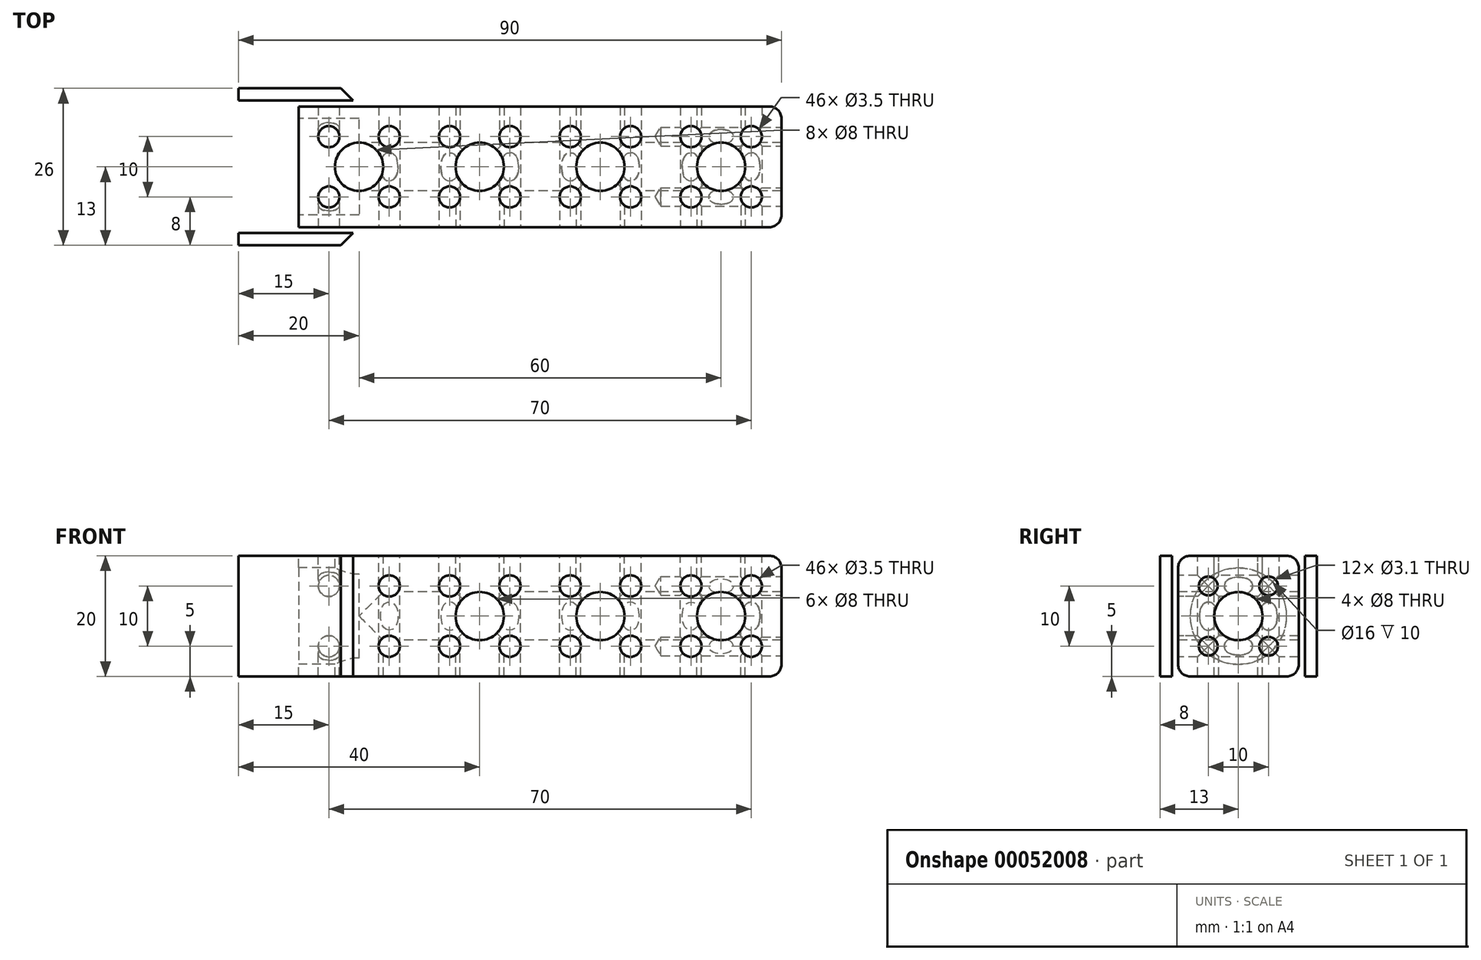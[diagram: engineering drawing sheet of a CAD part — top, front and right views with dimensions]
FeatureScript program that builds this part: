
annotation { "Feature Type Name" : "Feature", "Feature Type Description" : "" }
export const myFeature = defineFeature(function(context is Context, id is Id, definition is map)
    precondition{}
    {
        {
            var Q0;
            Q0=qCreatedBy(makeId("Top.planeOp"),FACE);
            var sketch = newSketch(context, id + "F0", { "sketchPlane" : qUnion([Q0])});
            skLineSegment(sketch, "E0.bottom", {"start": v(-10, 10) * mm, "end": v(70, 10) * mm});
            skLineSegment(sketch, "E0.top", {"start": v(-10, -10) * mm, "end": v(70, -10) * mm});
            skLineSegment(sketch, "E0.left", {"start": v(-10, 10) * mm, "end": v(-10, -10) * mm});
            skLineSegment(sketch, "E0.right", {"start": v(70, 10) * mm, "end": v(70, -10) * mm});
            skLineSegment(sketch, "E1.bottom", {"start": v(-10, -10) * mm, "end": v(0, -10) * mm});
            skLineSegment(sketch, "E1.top", {"start": v(-10, -11) * mm, "end": v(0, -11) * mm});
            skLineSegment(sketch, "E1.left", {"start": v(-10, -10) * mm, "end": v(-10, -11) * mm});
            skLineSegment(sketch, "E1.right", {"start": v(0, -10) * mm, "end": v(0, -11) * mm});
            skLineSegment(sketch, "E2.bottom", {"start": v(0, -11) * mm, "end": v(-20, -11) * mm});
            skLineSegment(sketch, "E2.top", {"start": v(0, -13) * mm, "end": v(-20, -13) * mm});
            skLineSegment(sketch, "E2.left", {"start": v(0, -11) * mm, "end": v(0, -13) * mm});
            skLineSegment(sketch, "E2.right", {"start": v(-20, -11) * mm, "end": v(-20, -13) * mm});
            skLineSegment(sketch, "E3.bottom", {"start": v(-10, 10) * mm, "end": v(0, 10) * mm});
            skLineSegment(sketch, "E3.top", {"start": v(-10, 11) * mm, "end": v(0, 11) * mm});
            skLineSegment(sketch, "E3.left", {"start": v(-10, 10) * mm, "end": v(-10, 11) * mm});
            skLineSegment(sketch, "E3.right", {"start": v(0, 10) * mm, "end": v(0, 11) * mm});
            skLineSegment(sketch, "E4.bottom", {"start": v(0, 11) * mm, "end": v(-20, 11) * mm});
            skLineSegment(sketch, "E4.top", {"start": v(0, 13) * mm, "end": v(-20, 13) * mm});
            skLineSegment(sketch, "E4.left", {"start": v(0, 11) * mm, "end": v(0, 13) * mm});
            skLineSegment(sketch, "E4.right", {"start": v(-20, 11) * mm, "end": v(-20, 13) * mm});
            skSolve(sketch);
        }
        {
            var Q0;
            Q0=makeQuery(id+"F0.imprint","IMPRINT",FACE,{"disambiguationData":[TD([[makeQuery(id+"F0.imprint","IMPRINT",EDGE,{"derivedFrom":sQuery(id+"F0.wireOp",EDGE,"E0.bottom")}),-1.0]])]});
            var Q1;
            Q1=makeQuery(id+"F0.imprint","IMPRINT",FACE,{"disambiguationData":[TD([[makeQuery(id+"F0.imprint","IMPRINT",EDGE,{"derivedFrom":sQuery(id+"F0.wireOp",EDGE,"E3.bottom")}),1.0]])]});
            var Q2;
            Q2=makeQuery(id+"F0.imprint","IMPRINT",FACE,{"disambiguationData":[TD([[makeQuery(id+"F0.imprint","IMPRINT",EDGE,{"derivedFrom":sQuery(id+"F0.wireOp",EDGE,"E4.top")}),1.0]])]});
            var Q3;
            Q3=makeQuery(id+"F0.imprint","IMPRINT",FACE,{"disambiguationData":[TD([[makeQuery(id+"F0.imprint","IMPRINT",EDGE,{"derivedFrom":sQuery(id+"F0.wireOp",EDGE,"E2.top")}),-1.0]])]});
            var Q4;
            Q4=makeQuery(id+"F0.imprint","IMPRINT",FACE,{"disambiguationData":[TD([[makeQuery(id+"F0.imprint","IMPRINT",EDGE,{"derivedFrom":sQuery(id+"F0.wireOp",EDGE,"E1.bottom")}),-1.0]])]});
            extrude(context, id + "F1", {"entities" : qUnion([Q0, Q1, Q2, Q3, Q4]), "endBound" : BoundingType.SYMMETRIC, "depth" : 20 * mm});
        }
        {
            var Q0;
            Q0=makeQuery(id+"F1.opExtrude","CAP_FACE",FACE,{"disambiguationData":[OSD([sQuery(id+"F0.wireOp",EDGE,"E0.bottom"),sQuery(id+"F0.wireOp",EDGE,"E0.top"),sQuery(id+"F0.wireOp",EDGE,"E0.left"),sQuery(id+"F0.wireOp",EDGE,"E0.right"),sQuery(id+"F0.wireOp",EDGE,"E1.left"),sQuery(id+"F0.wireOp",EDGE,"E1.right"),sQuery(id+"F0.wireOp",EDGE,"E2.bottom"),sQuery(id+"F0.wireOp",EDGE,"E2.top"),sQuery(id+"F0.wireOp",EDGE,"E2.left"),sQuery(id+"F0.wireOp",EDGE,"E2.right"),sQuery(id+"F0.wireOp",EDGE,"E3.left"),sQuery(id+"F0.wireOp",EDGE,"E3.right"),sQuery(id+"F0.wireOp",EDGE,"E4.bottom"),sQuery(id+"F0.wireOp",EDGE,"E4.top"),sQuery(id+"F0.wireOp",EDGE,"E4.left"),sQuery(id+"F0.wireOp",EDGE,"E4.right")])],"isStart":false});
            var sketch = newSketch(context, id + "F2", { "sketchPlane" : qUnion([Q0])});
            skLineSegment(sketch, "E5.bottom", {"start": v(70, 10) * mm, "end": v(50, 10) * mm});
            skLineSegment(sketch, "E5.top", {"start": v(70, -10) * mm, "end": v(50, -10) * mm});
            skLineSegment(sketch, "E5.left", {"start": v(70, 10) * mm, "end": v(70, -10) * mm});
            skLineSegment(sketch, "E5.right", {"start": v(50, 10) * mm, "end": v(50, -10) * mm});
            skLineSegment(sketch, "E6", {"start": v(50, 10) * mm, "end": v(70, -10) * mm});
            skLineSegment(sketch, "E7", {"start": v(60, 0) * mm, "end": v(70, 10) * mm});
            skLineSegment(sketch, "E8", {"start": v(60, 0) * mm, "end": v(50, -10) * mm});
            skPoint(sketch, "E9", {"position": v(55, -5) * mm});
            skLineSegment(sketch, "E10", {"start": v(60, 0) * mm, "end": v(50, 10) * mm});
            skLineSegment(sketch, "E11", {"start": v(60, 0) * mm, "end": v(70, -10) * mm});
            skPoint(sketch, "E12", {"position": v(55, 5) * mm});
            skPoint(sketch, "E13", {"position": v(65, -5) * mm});
            skPoint(sketch, "E14", {"position": v(65, 5) * mm});
            skPoint(sketch, "E15.1.0.0", {"position": v(35, -5) * mm});
            skPoint(sketch, "E15.1.0.1", {"position": v(45, -5) * mm});
            skPoint(sketch, "E15.1.0.2", {"position": v(45, 5) * mm});
            skPoint(sketch, "E15.1.0.3", {"position": v(35, 5) * mm});
            skPoint(sketch, "E15.2.0.0", {"position": v(15, -5) * mm});
            skPoint(sketch, "E15.2.0.1", {"position": v(25, -5) * mm});
            skPoint(sketch, "E15.2.0.2", {"position": v(25, 5) * mm});
            skPoint(sketch, "E15.2.0.3", {"position": v(15, 5) * mm});
            skPoint(sketch, "E15.3.0.0", {"position": v(-5, -5) * mm});
            skPoint(sketch, "E15.3.0.1", {"position": v(5, -5) * mm});
            skPoint(sketch, "E15.3.0.2", {"position": v(5, 5) * mm});
            skPoint(sketch, "E15.3.0.3", {"position": v(-5, 5) * mm});
            skLineSegment(sketch, "E15.direction1", {"start": v(55, -5) * mm, "end": v(35, -5) * mm, "construction": true});
            skSolve(sketch);
        }
        {
            var Q0;
            Q0=sQuery(id+"F2.wireOp",VERTEX,"E15.3.0.3");
            var Q1;
            Q1=sQuery(id+"F2.wireOp",VERTEX,"E15.3.0.2");
            var Q2;
            Q2=sQuery(id+"F2.wireOp",VERTEX,"E15.2.0.3");
            var Q3;
            Q3=sQuery(id+"F2.wireOp",VERTEX,"E15.3.0.0");
            var Q4;
            Q4=sQuery(id+"F2.wireOp",VERTEX,"E15.3.0.1");
            var Q5;
            Q5=sQuery(id+"F2.wireOp",VERTEX,"E15.2.0.0");
            var Q6;
            Q6=sQuery(id+"F2.wireOp",VERTEX,"E15.2.0.1");
            var Q7;
            Q7=sQuery(id+"F2.wireOp",VERTEX,"E15.1.0.1");
            var Q8;
            Q8=sQuery(id+"F2.wireOp",VERTEX,"E9");
            var Q9;
            Q9=sQuery(id+"F2.wireOp",VERTEX,"E13");
            var Q10;
            Q10=sQuery(id+"F2.wireOp",VERTEX,"E14");
            var Q11;
            Q11=sQuery(id+"F2.wireOp",VERTEX,"E12");
            var Q12;
            Q12=sQuery(id+"F2.wireOp",VERTEX,"E15.1.0.2");
            var Q13;
            Q13=sQuery(id+"F2.wireOp",VERTEX,"E15.1.0.3");
            var Q14;
            Q14=sQuery(id+"F2.wireOp",VERTEX,"E15.2.0.2");
            var Q15;
            Q15=sQuery(id+"F2.wireOp",VERTEX,"E15.1.0.0");
            var Q16;
            Q16=makeQuery(id+"F1.opExtrude","SWEPT_BODY",BODY,{"disambiguationData":[OSD([sQuery(id+"F0.wireOp",EDGE,"E0.bottom"),sQuery(id+"F0.wireOp",EDGE,"E0.top"),sQuery(id+"F0.wireOp",EDGE,"E0.left"),sQuery(id+"F0.wireOp",EDGE,"E0.right"),sQuery(id+"F0.wireOp",EDGE,"E1.left"),sQuery(id+"F0.wireOp",EDGE,"E1.right"),sQuery(id+"F0.wireOp",EDGE,"E2.bottom"),sQuery(id+"F0.wireOp",EDGE,"E2.top"),sQuery(id+"F0.wireOp",EDGE,"E2.left"),sQuery(id+"F0.wireOp",EDGE,"E2.right"),sQuery(id+"F0.wireOp",EDGE,"E3.left"),sQuery(id+"F0.wireOp",EDGE,"E3.right"),sQuery(id+"F0.wireOp",EDGE,"E4.bottom"),sQuery(id+"F0.wireOp",EDGE,"E4.top"),sQuery(id+"F0.wireOp",EDGE,"E4.left"),sQuery(id+"F0.wireOp",EDGE,"E4.right")])]});
            hole(context, id + "F3", {"style" : HoleStyle.SIMPLE, "endStyle" : HoleEndStyle.THROUGH, "holeDiameter" : 3.5 * mm, "locations" : qUnion([Q0, Q1, Q2, Q3, Q4, Q5, Q6, Q7, Q8, Q9, Q10, Q11, Q12, Q13, Q14, Q15]), "scope" : qUnion([Q16]), "isTappedThrough" : true});
        }
        {
            var Q0;
            Q0=makeQuery(id+"F1.opExtrude","SWEPT_FACE",FACE,{"disambiguationData":[OSD([sQuery(id+"F0.wireOp",EDGE,"E0.top")])]});
            var sketch = newSketch(context, id + "F4", { "sketchPlane" : qUnion([Q0])});
            skLineSegment(sketch, "E16.bottom", {"start": v(70, 10) * mm, "end": v(50, 10) * mm});
            skLineSegment(sketch, "E16.top", {"start": v(70, -10) * mm, "end": v(50, -10) * mm});
            skLineSegment(sketch, "E16.left", {"start": v(70, 10) * mm, "end": v(70, -10) * mm});
            skLineSegment(sketch, "E16.right", {"start": v(50, 10) * mm, "end": v(50, -10) * mm});
            skLineSegment(sketch, "E17", {"start": v(70, -10) * mm, "end": v(50, 10) * mm});
            skLineSegment(sketch, "E18", {"start": v(60, 0) * mm, "end": v(50, 10) * mm});
            skLineSegment(sketch, "E19", {"start": v(60, 0) * mm, "end": v(70, 10) * mm});
            skLineSegment(sketch, "E20", {"start": v(60, 0) * mm, "end": v(70, -10) * mm});
            skLineSegment(sketch, "E21", {"start": v(60, 0) * mm, "end": v(50, -10) * mm});
            skPoint(sketch, "E22", {"position": v(55, -5) * mm});
            skPoint(sketch, "E23", {"position": v(55, 5) * mm});
            skPoint(sketch, "E24", {"position": v(65, 5) * mm});
            skPoint(sketch, "E25", {"position": v(65, -5) * mm});
            skPoint(sketch, "E26.1.0.0", {"position": v(35, -5) * mm});
            skPoint(sketch, "E26.1.0.1", {"position": v(35, 5) * mm});
            skPoint(sketch, "E26.1.0.2", {"position": v(45, 5) * mm});
            skPoint(sketch, "E26.1.0.3", {"position": v(45, -5) * mm});
            skPoint(sketch, "E26.2.0.0", {"position": v(15, -5) * mm});
            skPoint(sketch, "E26.2.0.1", {"position": v(15, 5) * mm});
            skPoint(sketch, "E26.2.0.2", {"position": v(25, 5) * mm});
            skPoint(sketch, "E26.2.0.3", {"position": v(25, -5) * mm});
            skPoint(sketch, "E26.3.0.0", {"position": v(-5, -5) * mm});
            skPoint(sketch, "E26.3.0.1", {"position": v(-5, 5) * mm});
            skPoint(sketch, "E26.3.0.2", {"position": v(5, 5) * mm});
            skPoint(sketch, "E26.3.0.3", {"position": v(5, -5) * mm});
            skLineSegment(sketch, "E26.direction1", {"start": v(55, -5) * mm, "end": v(35, -5) * mm, "construction": true});
            skSolve(sketch);
        }
        {
            var Q0;
            Q0=sQuery(id+"F4.wireOp",VERTEX,"E26.3.0.2");
            var Q1;
            Q1=sQuery(id+"F4.wireOp",VERTEX,"E26.3.0.3");
            var Q2;
            Q2=sQuery(id+"F4.wireOp",VERTEX,"E26.2.0.0");
            var Q3;
            Q3=sQuery(id+"F4.wireOp",VERTEX,"E26.2.0.1");
            var Q4;
            Q4=sQuery(id+"F4.wireOp",VERTEX,"E26.2.0.2");
            var Q5;
            Q5=sQuery(id+"F4.wireOp",VERTEX,"E26.2.0.3");
            var Q6;
            Q6=sQuery(id+"F4.wireOp",VERTEX,"E26.1.0.0");
            var Q7;
            Q7=sQuery(id+"F4.wireOp",VERTEX,"E26.1.0.2");
            var Q8;
            Q8=sQuery(id+"F4.wireOp",VERTEX,"E22");
            var Q9;
            Q9=sQuery(id+"F4.wireOp",VERTEX,"E23");
            var Q10;
            Q10=sQuery(id+"F4.wireOp",VERTEX,"E24");
            var Q11;
            Q11=sQuery(id+"F4.wireOp",VERTEX,"E25");
            var Q12;
            Q12=sQuery(id+"F4.wireOp",VERTEX,"E26.1.0.3");
            var Q13;
            Q13=sQuery(id+"F4.wireOp",VERTEX,"E26.1.0.1");
            var Q14;
            Q14=makeQuery(id+"F1.opExtrude","SWEPT_BODY",BODY,{"disambiguationData":[OSD([sQuery(id+"F0.wireOp",EDGE,"E0.bottom"),sQuery(id+"F0.wireOp",EDGE,"E0.top"),sQuery(id+"F0.wireOp",EDGE,"E0.left"),sQuery(id+"F0.wireOp",EDGE,"E0.right"),sQuery(id+"F0.wireOp",EDGE,"E1.left"),sQuery(id+"F0.wireOp",EDGE,"E1.right"),sQuery(id+"F0.wireOp",EDGE,"E2.bottom"),sQuery(id+"F0.wireOp",EDGE,"E2.top"),sQuery(id+"F0.wireOp",EDGE,"E2.left"),sQuery(id+"F0.wireOp",EDGE,"E2.right"),sQuery(id+"F0.wireOp",EDGE,"E3.left"),sQuery(id+"F0.wireOp",EDGE,"E3.right"),sQuery(id+"F0.wireOp",EDGE,"E4.bottom"),sQuery(id+"F0.wireOp",EDGE,"E4.top"),sQuery(id+"F0.wireOp",EDGE,"E4.left"),sQuery(id+"F0.wireOp",EDGE,"E4.right")])]});
            hole(context, id + "F5", {"style" : HoleStyle.SIMPLE, "endStyle" : HoleEndStyle.THROUGH, "holeDiameter" : 3.5 * mm, "locations" : qUnion([Q0, Q1, Q2, Q3, Q4, Q5, Q6, Q7, Q8, Q9, Q10, Q11, Q12, Q13]), "scope" : qUnion([Q14]), "isTappedThrough" : true});
        }
        {
            var Q0;
            Q0=makeQuery(id+"F1.opExtrude","SWEPT_FACE",FACE,{"disambiguationData":[OSD([sQuery(id+"F0.wireOp",EDGE,"E2.top")])]});
            var sketch = newSketch(context, id + "F6", { "sketchPlane" : qUnion([Q0])});
            skLineSegment(sketch, "E27.bottom", {"start": v(-15, 5) * mm, "end": v(-5, 5) * mm});
            skLineSegment(sketch, "E27.top", {"start": v(-15, -5) * mm, "end": v(-5, -5) * mm});
            skLineSegment(sketch, "E27.left", {"start": v(-15, 5) * mm, "end": v(-15, -5) * mm});
            skLineSegment(sketch, "E27.right", {"start": v(-5, 5) * mm, "end": v(-5, -5) * mm});
            skLineSegment(sketch, "E28", {"start": v(-10, 10) * mm, "end": v(-10, 5) * mm});
            skLineSegment(sketch, "E29", {"start": v(0, 0) * mm, "end": v(-5, 0) * mm});
            skPoint(sketch, "E30", {"position": v(-5, 0) * mm});
            skPoint(sketch, "E31", {"position": v(-10, 5) * mm});
            skSolve(sketch);
        }
        {
            var Q0;
            Q0=sQuery(id+"F6.wireOp",VERTEX,"E27.left.start");
            var Q1;
            Q1=sQuery(id+"F6.wireOp",VERTEX,"E27.bottom.end");
            var Q2;
            Q2=sQuery(id+"F6.wireOp",VERTEX,"E27.right.end");
            var Q3;
            Q3=sQuery(id+"F6.wireOp",VERTEX,"E27.top.start");
            var Q4;
            Q4=makeQuery(id+"F1.opExtrude","SWEPT_BODY",BODY,{"disambiguationData":[OSD([sQuery(id+"F0.wireOp",EDGE,"E0.bottom"),sQuery(id+"F0.wireOp",EDGE,"E0.top"),sQuery(id+"F0.wireOp",EDGE,"E0.left"),sQuery(id+"F0.wireOp",EDGE,"E0.right"),sQuery(id+"F0.wireOp",EDGE,"E1.left"),sQuery(id+"F0.wireOp",EDGE,"E1.right"),sQuery(id+"F0.wireOp",EDGE,"E2.bottom"),sQuery(id+"F0.wireOp",EDGE,"E2.top"),sQuery(id+"F0.wireOp",EDGE,"E2.left"),sQuery(id+"F0.wireOp",EDGE,"E2.right"),sQuery(id+"F0.wireOp",EDGE,"E3.left"),sQuery(id+"F0.wireOp",EDGE,"E3.right"),sQuery(id+"F0.wireOp",EDGE,"E4.bottom"),sQuery(id+"F0.wireOp",EDGE,"E4.top"),sQuery(id+"F0.wireOp",EDGE,"E4.left"),sQuery(id+"F0.wireOp",EDGE,"E4.right")])]});
            hole(context, id + "F7", {"style" : HoleStyle.SIMPLE, "endStyle" : HoleEndStyle.THROUGH, "holeDiameter" : 3.5 * mm, "locations" : qUnion([Q0, Q1, Q2, Q3]), "scope" : qUnion([Q4]), "isTappedThrough" : true});
        }
        {
            var Q0;
            Q0=makeQuery(id+"F1.opExtrude","SWEPT_EDGE",EDGE,{"disambiguationData":[OSD([sQuery(id+"F0.wireOp",EDGE,"E2.top"),sQuery(id+"F0.wireOp",EDGE,"E2.left")])]});
            var Q1;
            Q1=makeQuery(id+"F1.opExtrude","SWEPT_EDGE",EDGE,{"disambiguationData":[OSD([sQuery(id+"F0.wireOp",EDGE,"E4.top"),sQuery(id+"F0.wireOp",EDGE,"E4.left")])]});
            chamfer(context, id + "F8", {"entities" : qUnion([Q0, Q1]), "width" : 3 * mm, "tangentPropagation" : true});
        }
        {
            var Q0;
            Q0=makeQuery(id+"F1.opExtrude","CAP_FACE",FACE,{"disambiguationData":[OSD([sQuery(id+"F0.wireOp",EDGE,"E0.bottom"),sQuery(id+"F0.wireOp",EDGE,"E0.top"),sQuery(id+"F0.wireOp",EDGE,"E0.left"),sQuery(id+"F0.wireOp",EDGE,"E0.right"),sQuery(id+"F0.wireOp",EDGE,"E1.left"),sQuery(id+"F0.wireOp",EDGE,"E1.right"),sQuery(id+"F0.wireOp",EDGE,"E2.bottom"),sQuery(id+"F0.wireOp",EDGE,"E2.top"),sQuery(id+"F0.wireOp",EDGE,"E2.left"),sQuery(id+"F0.wireOp",EDGE,"E2.right"),sQuery(id+"F0.wireOp",EDGE,"E3.left"),sQuery(id+"F0.wireOp",EDGE,"E3.right"),sQuery(id+"F0.wireOp",EDGE,"E4.bottom"),sQuery(id+"F0.wireOp",EDGE,"E4.top"),sQuery(id+"F0.wireOp",EDGE,"E4.left"),sQuery(id+"F0.wireOp",EDGE,"E4.right")])],"isStart":false});
            var sketch = newSketch(context, id + "F9", { "sketchPlane" : qUnion([Q0])});
            skLineSegment(sketch, "E32.bottom", {"start": v(70, -10) * mm, "end": v(50, -10) * mm});
            skLineSegment(sketch, "E32.top", {"start": v(70, 10) * mm, "end": v(50, 10) * mm});
            skLineSegment(sketch, "E32.left", {"start": v(70, -10) * mm, "end": v(70, 10) * mm});
            skLineSegment(sketch, "E32.right", {"start": v(50, -10) * mm, "end": v(50, 10) * mm});
            skLineSegment(sketch, "E33", {"start": v(50, 10) * mm, "end": v(70, -10) * mm});
            skPoint(sketch, "E34", {"position": v(60, 0) * mm});
            skPoint(sketch, "E35.1.0.0", {"position": v(40, 0) * mm});
            skPoint(sketch, "E35.2.0.0", {"position": v(20, 0) * mm});
            skPoint(sketch, "E35.3.0.0", {"position": v(0, 0) * mm});
            skLineSegment(sketch, "E35.direction1", {"start": v(60, 0) * mm, "end": v(40, 0) * mm, "construction": true});
            skSolve(sketch);
        }
        {
            var Q0;
            Q0=sQuery(id+"F9.wireOp",VERTEX,"E35.3.0.0");
            var Q1;
            Q1=sQuery(id+"F9.wireOp",VERTEX,"E35.2.0.0");
            var Q2;
            Q2=sQuery(id+"F9.wireOp",VERTEX,"E35.1.0.0");
            var Q3;
            Q3=sQuery(id+"F9.wireOp",VERTEX,"E34");
            var Q4;
            Q4=makeQuery(id+"F1.opExtrude","SWEPT_BODY",BODY,{"disambiguationData":[OSD([sQuery(id+"F0.wireOp",EDGE,"E0.bottom"),sQuery(id+"F0.wireOp",EDGE,"E0.top"),sQuery(id+"F0.wireOp",EDGE,"E0.left"),sQuery(id+"F0.wireOp",EDGE,"E0.right"),sQuery(id+"F0.wireOp",EDGE,"E1.left"),sQuery(id+"F0.wireOp",EDGE,"E1.right"),sQuery(id+"F0.wireOp",EDGE,"E2.bottom"),sQuery(id+"F0.wireOp",EDGE,"E2.top"),sQuery(id+"F0.wireOp",EDGE,"E2.left"),sQuery(id+"F0.wireOp",EDGE,"E2.right"),sQuery(id+"F0.wireOp",EDGE,"E3.left"),sQuery(id+"F0.wireOp",EDGE,"E3.right"),sQuery(id+"F0.wireOp",EDGE,"E4.bottom"),sQuery(id+"F0.wireOp",EDGE,"E4.top"),sQuery(id+"F0.wireOp",EDGE,"E4.left"),sQuery(id+"F0.wireOp",EDGE,"E4.right")])]});
            hole(context, id + "F10", {"style" : HoleStyle.SIMPLE, "endStyle" : HoleEndStyle.THROUGH, "holeDiameter" : 8 * mm, "locations" : qUnion([Q0, Q1, Q2, Q3]), "scope" : qUnion([Q4]), "isTappedThrough" : true});
        }
        {
            var Q0;
            Q0=makeQuery(id+"F1.opExtrude","SWEPT_FACE",FACE,{"disambiguationData":[OSD([sQuery(id+"F0.wireOp",EDGE,"E0.top")])]});
            var sketch = newSketch(context, id + "F11", { "sketchPlane" : qUnion([Q0])});
            skLineSegment(sketch, "E36.bottom", {"start": v(70, 10) * mm, "end": v(50, 10) * mm});
            skLineSegment(sketch, "E36.top", {"start": v(70, -10) * mm, "end": v(50, -10) * mm});
            skLineSegment(sketch, "E36.left", {"start": v(70, 10) * mm, "end": v(70, -10) * mm});
            skLineSegment(sketch, "E36.right", {"start": v(50, 10) * mm, "end": v(50, -10) * mm});
            skLineSegment(sketch, "E37", {"start": v(50, 10) * mm, "end": v(70, -10) * mm});
            skPoint(sketch, "E38", {"position": v(60, 0) * mm});
            skPoint(sketch, "E39.1.0.0", {"position": v(40, 0) * mm});
            skPoint(sketch, "E39.2.0.0", {"position": v(20, 0) * mm});
            skLineSegment(sketch, "E39.direction1", {"start": v(60, 0) * mm, "end": v(40, 0) * mm, "construction": true});
            skSolve(sketch);
        }
        {
            var Q0;
            Q0=sQuery(id+"F11.wireOp",VERTEX,"E39.2.0.0");
            var Q1;
            Q1=sQuery(id+"F11.wireOp",VERTEX,"E39.1.0.0");
            var Q2;
            Q2=sQuery(id+"F11.wireOp",VERTEX,"E38");
            var Q3;
            Q3=makeQuery(id+"F1.opExtrude","SWEPT_BODY",BODY,{"disambiguationData":[OSD([sQuery(id+"F0.wireOp",EDGE,"E0.bottom"),sQuery(id+"F0.wireOp",EDGE,"E0.top"),sQuery(id+"F0.wireOp",EDGE,"E0.left"),sQuery(id+"F0.wireOp",EDGE,"E0.right"),sQuery(id+"F0.wireOp",EDGE,"E1.left"),sQuery(id+"F0.wireOp",EDGE,"E1.right"),sQuery(id+"F0.wireOp",EDGE,"E2.bottom"),sQuery(id+"F0.wireOp",EDGE,"E2.top"),sQuery(id+"F0.wireOp",EDGE,"E2.left"),sQuery(id+"F0.wireOp",EDGE,"E2.right"),sQuery(id+"F0.wireOp",EDGE,"E3.left"),sQuery(id+"F0.wireOp",EDGE,"E3.right"),sQuery(id+"F0.wireOp",EDGE,"E4.bottom"),sQuery(id+"F0.wireOp",EDGE,"E4.top"),sQuery(id+"F0.wireOp",EDGE,"E4.left"),sQuery(id+"F0.wireOp",EDGE,"E4.right")])]});
            hole(context, id + "F12", {"style" : HoleStyle.SIMPLE, "endStyle" : HoleEndStyle.THROUGH, "holeDiameter" : 8 * mm, "locations" : qUnion([Q0, Q1, Q2]), "scope" : qUnion([Q3]), "isTappedThrough" : true});
        }
        {
            var Q0;
            Q0=makeQuery(id+"F1.opExtrude","SWEPT_FACE",FACE,{"disambiguationData":[OSD([sQuery(id+"F0.wireOp",EDGE,"E0.left"),sQuery(id+"F0.wireOp",EDGE,"E1.left"),sQuery(id+"F0.wireOp",EDGE,"E3.left")])]});
            var sketch = newSketch(context, id + "F13", { "sketchPlane" : qUnion([Q0])});
            skPoint(sketch, "E40", {"position": v(0, 0) * mm});
            skSolve(sketch);
        }
        {
            var Q0;
            Q0=sQuery(id+"F13.wireOp",VERTEX,"E40");
            var Q1;
            Q1=makeQuery(id+"F1.opExtrude","SWEPT_BODY",BODY,{"disambiguationData":[OSD([sQuery(id+"F0.wireOp",EDGE,"E0.bottom"),sQuery(id+"F0.wireOp",EDGE,"E0.top"),sQuery(id+"F0.wireOp",EDGE,"E0.left"),sQuery(id+"F0.wireOp",EDGE,"E0.right"),sQuery(id+"F0.wireOp",EDGE,"E1.left"),sQuery(id+"F0.wireOp",EDGE,"E1.right"),sQuery(id+"F0.wireOp",EDGE,"E2.bottom"),sQuery(id+"F0.wireOp",EDGE,"E2.top"),sQuery(id+"F0.wireOp",EDGE,"E2.left"),sQuery(id+"F0.wireOp",EDGE,"E2.right"),sQuery(id+"F0.wireOp",EDGE,"E3.left"),sQuery(id+"F0.wireOp",EDGE,"E3.right"),sQuery(id+"F0.wireOp",EDGE,"E4.bottom"),sQuery(id+"F0.wireOp",EDGE,"E4.top"),sQuery(id+"F0.wireOp",EDGE,"E4.left"),sQuery(id+"F0.wireOp",EDGE,"E4.right")])]});
            hole(context, id + "F14", {"style" : HoleStyle.C_BORE, "endStyle" : HoleEndStyle.THROUGH, "holeDiameter" : 8 * mm, "cBoreDiameter" : 16 * mm, "cBoreDepth" : 10 * mm, "locations" : qUnion([Q0]), "scope" : qUnion([Q1]), "isTappedThrough" : true});
        }
        {
            var Q0;
            Q0=makeQuery(id+"F1.opExtrude","SWEPT_FACE",FACE,{"disambiguationData":[OSD([sQuery(id+"F0.wireOp",EDGE,"E0.right")])]});
            var sketch = newSketch(context, id + "F15", { "sketchPlane" : qUnion([Q0])});
            skLineSegment(sketch, "E41.bottom", {"start": v(-5, 5) * mm, "end": v(5, 5) * mm});
            skLineSegment(sketch, "E41.top", {"start": v(-5, -5) * mm, "end": v(5, -5) * mm});
            skLineSegment(sketch, "E41.left", {"start": v(-5, 5) * mm, "end": v(-5, -5) * mm});
            skLineSegment(sketch, "E41.right", {"start": v(5, 5) * mm, "end": v(5, -5) * mm});
            skLineSegment(sketch, "E42", {"start": v(0, 0) * mm, "end": v(5, 0) * mm});
            skLineSegment(sketch, "E43", {"start": v(0, 0) * mm, "end": v(0, 5) * mm});
            skPoint(sketch, "E44", {"position": v(5, 0) * mm});
            skPoint(sketch, "E45", {"position": v(0, 5) * mm});
            skSolve(sketch);
        }
        {
            var Q0;
            Q0=sQuery(id+"F15.wireOp",VERTEX,"E41.left.start");
            var Q1;
            Q1=sQuery(id+"F15.wireOp",VERTEX,"E41.bottom.end");
            var Q2;
            Q2=sQuery(id+"F15.wireOp",VERTEX,"E41.top.end");
            var Q3;
            Q3=sQuery(id+"F15.wireOp",VERTEX,"E41.left.end");
            var Q4;
            Q4=makeQuery(id+"F1.opExtrude","SWEPT_BODY",BODY,{"disambiguationData":[OSD([sQuery(id+"F0.wireOp",EDGE,"E0.bottom"),sQuery(id+"F0.wireOp",EDGE,"E0.top"),sQuery(id+"F0.wireOp",EDGE,"E0.left"),sQuery(id+"F0.wireOp",EDGE,"E0.right"),sQuery(id+"F0.wireOp",EDGE,"E1.left"),sQuery(id+"F0.wireOp",EDGE,"E1.right"),sQuery(id+"F0.wireOp",EDGE,"E2.bottom"),sQuery(id+"F0.wireOp",EDGE,"E2.top"),sQuery(id+"F0.wireOp",EDGE,"E2.left"),sQuery(id+"F0.wireOp",EDGE,"E2.right"),sQuery(id+"F0.wireOp",EDGE,"E3.left"),sQuery(id+"F0.wireOp",EDGE,"E3.right"),sQuery(id+"F0.wireOp",EDGE,"E4.bottom"),sQuery(id+"F0.wireOp",EDGE,"E4.top"),sQuery(id+"F0.wireOp",EDGE,"E4.left"),sQuery(id+"F0.wireOp",EDGE,"E4.right")])]});
            hole(context, id + "F16", {"style" : HoleStyle.SIMPLE, "endStyle" : HoleEndStyle.BLIND, "holeDiameter" : 3.1 * mm, "holeDepth" : 20 * mm, "locations" : qUnion([Q0, Q1, Q2, Q3]), "scope" : qUnion([Q4])});
        }
        {
            var Q0;
            Q0=makeQuery(id+"F1.opExtrude","CAP_EDGE",EDGE,{"disambiguationData":[OSD([sQuery(id+"F0.wireOp",EDGE,"E0.top")])],"isStart":true});
            var Q1;
            Q1=makeQuery(id+"F1.opExtrude","CAP_EDGE",EDGE,{"disambiguationData":[OSD([sQuery(id+"F0.wireOp",EDGE,"E0.top")])],"isStart":false});
            var Q2;
            Q2=makeQuery(id+"F1.opExtrude","CAP_EDGE",EDGE,{"disambiguationData":[OSD([sQuery(id+"F0.wireOp",EDGE,"E0.bottom")])],"isStart":true});
            var Q3;
            Q3=makeQuery(id+"F1.opExtrude","CAP_EDGE",EDGE,{"disambiguationData":[OSD([sQuery(id+"F0.wireOp",EDGE,"E0.bottom")])],"isStart":false});
            var Q4;
            Q4=makeQuery(id+"F1.opExtrude","SWEPT_EDGE",EDGE,{"disambiguationData":[OSD([sQuery(id+"F0.wireOp",EDGE,"E0.bottom"),sQuery(id+"F0.wireOp",EDGE,"E0.right")])]});
            var Q5;
            Q5=makeQuery(id+"F1.opExtrude","CAP_EDGE",EDGE,{"disambiguationData":[OSD([sQuery(id+"F0.wireOp",EDGE,"E0.right")])],"isStart":false});
            var Q6;
            Q6=makeQuery(id+"F1.opExtrude","SWEPT_EDGE",EDGE,{"disambiguationData":[OSD([sQuery(id+"F0.wireOp",EDGE,"E0.top"),sQuery(id+"F0.wireOp",EDGE,"E0.right")])]});
            var Q7;
            Q7=makeQuery(id+"F1.opExtrude","CAP_EDGE",EDGE,{"disambiguationData":[OSD([sQuery(id+"F0.wireOp",EDGE,"E0.right")])],"isStart":true});
            fillet(context, id + "F17", {"entities" : qUnion([Q0, Q1, Q2, Q3, Q4, Q5, Q6, Q7]), "radius" : 2 * mm, "tangentPropagation" : true, "allowEdgeOverflow" : false});
        }
    });
